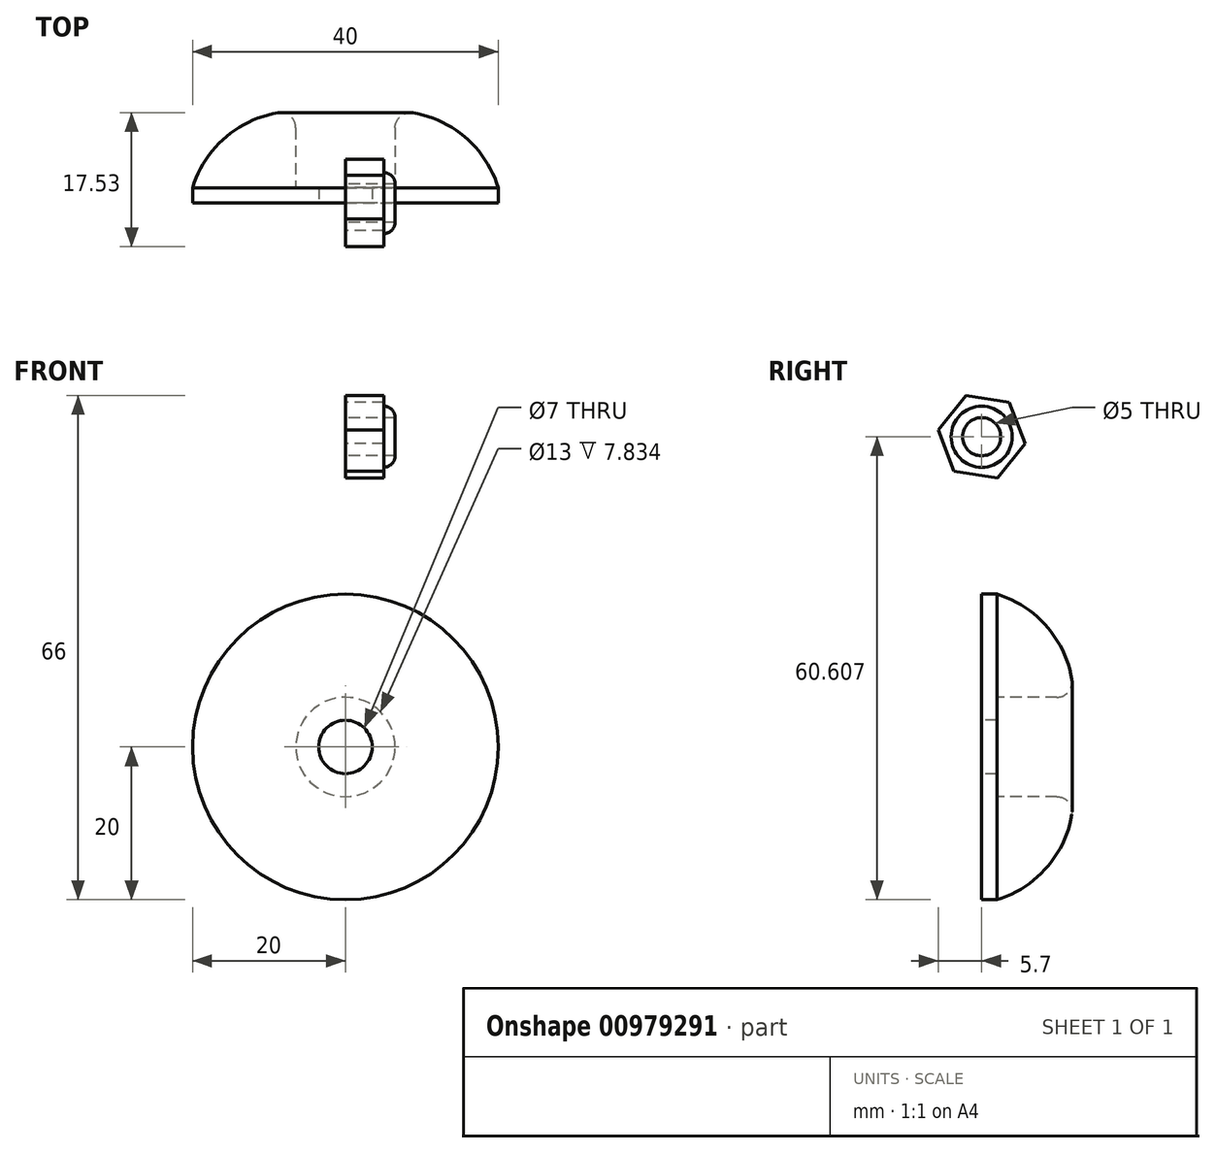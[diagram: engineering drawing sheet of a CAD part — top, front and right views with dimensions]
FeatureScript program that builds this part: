
annotation { "Feature Type Name" : "Feature", "Feature Type Description" : "" }
export const myFeature = defineFeature(function(context is Context, id is Id, definition is map)
    precondition{}
    {
        {
            var Q0;
            Q0=qCreatedBy(makeId("Right.planeOp"),FACE);
            var sketch = newSketch(context, id + "F0", { "sketchPlane" : qUnion([Q0])});
            skLineSegment(sketch, "E0", {"start": v(0, 0) * mm, "end": v(54.51, 0) * mm, "construction": true});
            skLineSegment(sketch, "E1", {"start": v(0, 3.5) * mm, "end": v(2, 3.5) * mm});
            skLineSegment(sketch, "E2", {"start": v(2, 3.5) * mm, "end": v(2, 6.5) * mm});
            skLineSegment(sketch, "E3", {"start": v(2, 6.5) * mm, "end": v(9.83, 6.5) * mm});
            skLineSegment(sketch, "E4", {"start": v(0, 3.5) * mm, "end": v(0, 20) * mm});
            skLineSegment(sketch, "E5", {"start": v(0, 20) * mm, "end": v(2, 20) * mm});
            skArc(sketch, "E6", {"start": v(11.8, 8.83) * mm, "mid": v(8.5, 15.81) * mm, "end": v(2, 20) * mm});
            skPoint(sketch, "E7.visualSharp", {"position": v(12, 6.5) * mm});
            skArc(sketch, "E7.filletArc", {"start": v(9.83, 6.5) * mm, "mid": v(11.36, 7.2) * mm, "end": v(11.8, 8.83) * mm});
            skSolve(sketch);
        }
        {
            var Q0;
            Q0 = qSketchRegion(id + "F0", true);
            var Q1;
            Q1=sQuery(id+"F0.wireOp",EDGE,"E0");
            revolve(context, id + "F1", {"surfaceOperationType" : NewSurfaceOperationType.NEW, "entities" : qUnion([Q0]), "axis" : qUnion([Q1]), "revolveType" : RevolveType.FULL});
        }
        {
            var Q0;
            Q0=qCreatedBy(makeId("Right.planeOp"),FACE);
            var sketch = newSketch(context, id + "F2", { "sketchPlane" : qUnion([Q0])});
            skCircle(sketch, "E8.cCircle", {"center": v(0, 40.6) * mm, "radius": 5 * mm, "construction": true});
            skLineSegment(sketch, "E8.0", {"start": v(-5.7, 41.51) * mm, "end": v(-2.07, 46) * mm});
            skLineSegment(sketch, "E8.1", {"start": v(-2.07, 46) * mm, "end": v(3.63, 45.1) * mm});
            skLineSegment(sketch, "E8.2", {"start": v(3.63, 45.1) * mm, "end": v(5.7, 39.7) * mm});
            skLineSegment(sketch, "E8.3", {"start": v(5.7, 39.7) * mm, "end": v(2.07, 35.22) * mm});
            skLineSegment(sketch, "E8.4", {"start": v(2.07, 35.22) * mm, "end": v(-3.63, 36.12) * mm});
            skLineSegment(sketch, "E8.5", {"start": v(-3.63, 36.12) * mm, "end": v(-5.7, 41.51) * mm});
            skPoint(sketch, "E8.0.midPoint", {"position": v(-3.88, 43.75) * mm});
            skCircle(sketch, "E9", {"center": v(0, 40.6) * mm, "radius": 2.5 * mm});
            skSolve(sketch);
        }
        {
            var Q0;
            Q0=makeQuery(id+"F2.imprint","IMPRINT",FACE,{"disambiguationData":[TD([[makeQuery(id+"F2.imprint","IMPRINT",EDGE,{"derivedFrom":sQuery(id+"F2.wireOp",EDGE,"E8.0")}),-1.0]])]});
            extrude(context, id + "F3", {"entities" : qUnion([Q0]), "depth" : 5 * mm, "offsetDistance" : 25 * mm});
        }
        {
            var Q0;
            Q0=qCreatedBy(makeId("Front.planeOp"),FACE);
            var sketch = newSketch(context, id + "F4", { "sketchPlane" : qUnion([Q0])});
            skLineSegment(sketch, "E10", {"start": v(0, 43.1) * mm, "end": v(0, 38.1) * mm, "construction": true});
            skLineSegment(sketch, "E11", {"start": v(5, 38.1) * mm, "end": v(0, 38.1) * mm});
            skLineSegment(sketch, "E12", {"start": v(0, 43.1) * mm, "end": v(5, 43.1) * mm});
            skLineSegment(sketch, "E13", {"start": v(0, 40.6) * mm, "end": v(7.73, 40.6) * mm, "construction": true});
            skLineSegment(sketch, "E14", {"start": v(5, 43.1) * mm, "end": v(6.5, 43.1) * mm});
            skLineSegment(sketch, "E15", {"start": v(5, 43.1) * mm, "end": v(5, 44.6) * mm});
            skArc(sketch, "E16", {"start": v(6.5, 43.1) * mm, "mid": v(6.06, 44.17) * mm, "end": v(5, 44.6) * mm});
            skSolve(sketch);
        }
        {
            var Q0;
            Q0=makeQuery(id+"F4.imprint","IMPRINT",FACE,{"disambiguationData":[TD([[makeQuery(id+"F4.imprint","IMPRINT",EDGE,{"derivedFrom":sQuery(id+"F4.wireOp",EDGE,"E14")}),1.0]])]});
            var Q1;
            Q1=sQuery(id+"F4.wireOp",EDGE,"E13");
            revolve(context, id + "F5", {"operationType" : NewBodyOperationType.ADD, "surfaceOperationType" : NewSurfaceOperationType.NEW, "entities" : qUnion([Q0]), "axis" : qUnion([Q1]), "revolveType" : RevolveType.FULL});
        }
    });
